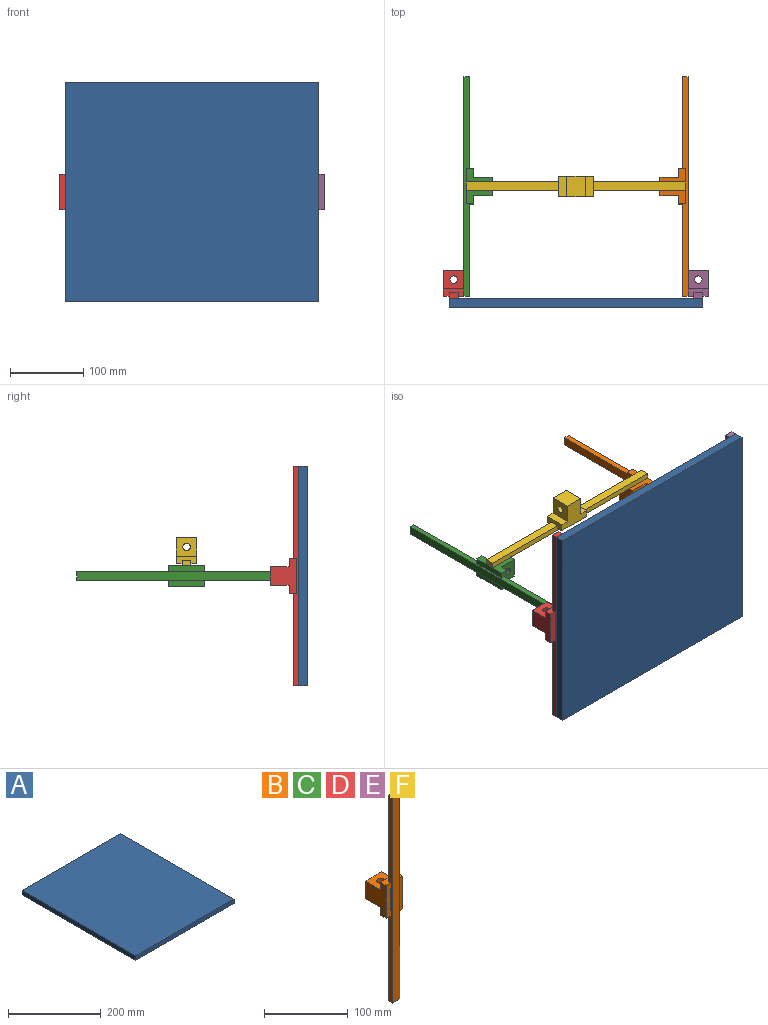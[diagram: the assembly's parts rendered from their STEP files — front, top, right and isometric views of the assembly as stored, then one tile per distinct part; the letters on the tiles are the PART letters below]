
ASSEMBLY  parts=6 mates=5
PART A: 6 faces, bbox 300x346x12 mm
  f0: plane 346x12mm, normal (1,0,0), area 4152mm2, adj f1,f3,f4,f5
  f1: plane 300x12mm, normal (0,1,0), area 3600mm2, adj f0,f2,f4,f5
  f2: plane 346x12mm, normal (-1,0,0), area 4152mm2, adj f1,f3,f4,f5
  f3: plane 300x12mm, normal (0,-1,0), area 3600mm2, adj f0,f2,f4,f5
  f4: plane 346x300mm, normal (0,0,1), area 103800mm2, adj f0,f1,f2,f3
  f5: plane 346x300mm, normal (0,0,-1), area 103800mm2, adj f0,f1,f2,f3
PART B: 19 faces, bbox 28x38.4x300 mm
  f0: plane 28x11.3mm, normal (0,1,0), area 316.4mm2, adj f9,f11,f14,f16
  f1: plane 126x12mm, normal (0,1,0), area 1512mm2, adj f3,f5,f7,f11
  f2: plane 126x12mm, normal (0,1,0), area 1512mm2, adj f3,f5,f6,f8
  f3: plane 300x7.5mm, normal (-1,0,0), area 2034mm2, adj f1,f2,f4,f6,f7,f8,f10,f11
  f4: plane 300x12mm, normal (0,-1,0), area 3600mm2, adj f3,f5,f6,f7
  f5: plane 300x7.5mm, normal (1,0,0), area 2034mm2, adj f1,f2,f4,f6,f7,f8,f11,f12
  f6: plane 12x7.5mm, normal (0,0,1), area 90mm2, adj f2,f3,f4,f5
  f7: plane 12x7.5mm, normal (0,0,-1), area 90mm2, adj f1,f3,f4,f5
  f8: plane 28x10mm, normal (0,0,1), area 226mm2, adj f2,f3,f5,f9,f10,f12,f13,f14
  f9: plane 48x35.4mm, normal (-1,0,0), area 1125.2mm2, adj f0,f8,f10,f11,f13,f15,f16,f18
  f10: plane 48x8mm, normal (0,-1,0), area 384mm2, adj f3,f8,f9,f11
  f11: plane 28x10mm, normal (0,0,-1), area 226mm2, adj f0,f1,f3,f5,f9,f10,f12,f14
  f12: plane 48x8mm, normal (0,-1,0), area 384mm2, adj f5,f8,f11,f14
  f13: plane 28x11.3mm, normal (0,1,0), area 316.4mm2, adj f8,f9,f14,f15
  f14: plane 48x35.4mm, normal (1,0,0), area 1125.2mm2, adj f0,f8,f11,f12,f13,f15,f16,f18
  f15: plane 28x25.4mm, normal (0,0,1), area 629.5mm2, adj f9,f13,f14,f17,f18
  f16: plane 28x25.4mm, normal (0,0,-1), area 629.5mm2, adj f0,f9,f14,f17,f18
  f17: cylinder r=5.1mm len=25.4mm, axis (0,0,-1), area 813.9mm2, adj f15,f16
  f18: plane 28x25.4mm, normal (0,1,0), area 711.2mm2, adj f9,f14,f15,f16
PART C: same geometry as B
PART D: same geometry as B
PART E: same geometry as B
PART F: same geometry as B
PLACE A rot(axis=(-0.58,-0.58,-0.58),120deg) t=(167,-12,150)mm
PLACE B rot(axis=(-0.58,0.58,0.58),120deg) t=(340,153,150)mm
PLACE C rot(axis=(-0.58,-0.58,-0.58),120deg) t=(-6,153,150)mm
PLACE D t=(0,-20,150)mm
PLACE E rot(axis=(0,-1,0),180deg) t=(334,-20,150)mm
PLACE F rot(axis=(0.58,0.58,0.58),120deg) t=(167,153,144)mm
MATE fastened E.f14 <-> B.f4  axis (-1,0,0) through (320,3,150)mm
MATE fastened A.f4 <-> D.f4  axis (0,1,0) through (-6,0,300)mm
MATE fastened F.f4 <-> B.f9  axis (0,0,-1) through (317,153,164)mm
MATE fastened F.f4 <-> C.f14  axis (0,0,-1) through (17,153,164)mm
MATE fastened C.f4 <-> D.f14  axis (-1,0,0) through (14,3,150)mm
